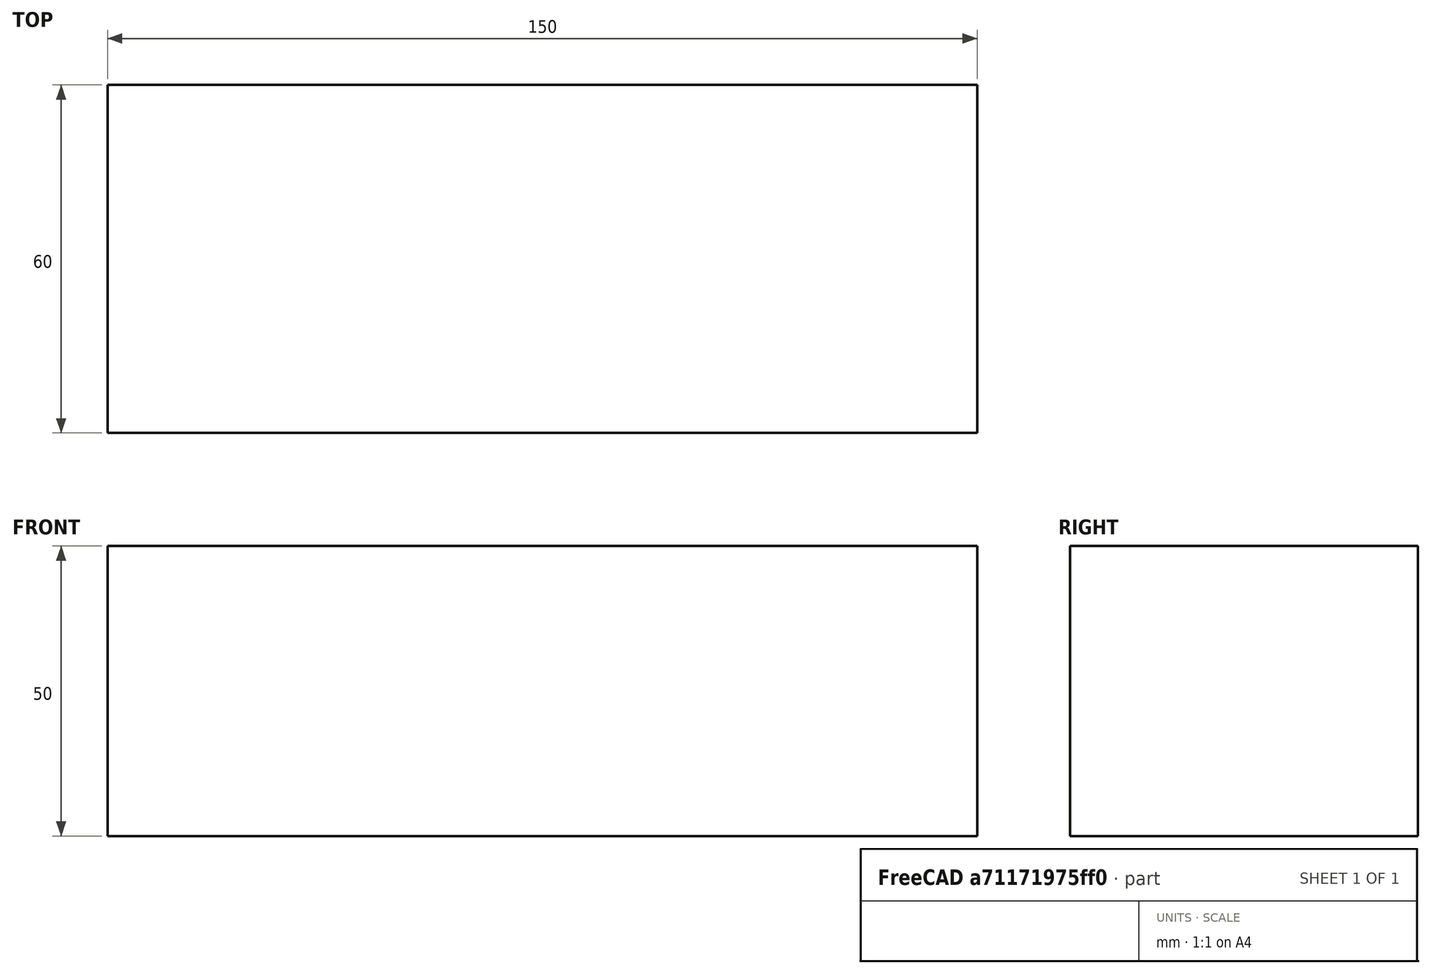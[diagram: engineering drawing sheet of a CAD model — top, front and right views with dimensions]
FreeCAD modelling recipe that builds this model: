
FCSTD DOCUMENT  (FreeCAD 0.15R4671 (Git))
Label: Flat Bar 150x60 EN10058 S235JR
License: All rights reserved
LicenseURL: http://en.wikipedia.org/wiki/All_rights_reserved
objects: Sketcher::SketchObject×1, Part::Extrusion×1
note: 2 computed .brp shape members not serialized (recipe doc carries the construction recipe); baked Part::Feature solids carry a one-line shape summary decoded from their .brp

FEATURE [Sketcher::SketchObject] Sketch
  sketch-geometry (4):
    g0: LineSegment StartX=-75 StartY=-30 StartZ=0 EndX=75 EndY=-30 EndZ=0
    g1: LineSegment StartX=75 StartY=-30 StartZ=0 EndX=75 EndY=30 EndZ=0
    g2: LineSegment StartX=75 StartY=30 StartZ=0 EndX=-75 EndY=30 EndZ=0
    g3: LineSegment StartX=-75 StartY=30 StartZ=0 EndX=-75 EndY=-30 EndZ=0
  constraints (12):
    c: Coincident(g0,g1)
    c: Coincident(g1,g2)
    c: Coincident(g2,g3)
    c: Coincident(g3,g0)
    c: Horizontal(g0)
    c: Horizontal(g2)
    c: Vertical(g1)
    c: Vertical(g3)
    c: Symmetric(g1,g2,g-2)
    c: Symmetric(g0,g1,g-1)
    c: DistanceY(g1) = 60
    c: DistanceX(g0) = 150
FEATURE [Part::Extrusion] Extrude  label="Flat Bar 150x60 EN10058 S235JR"
  Base = -> Sketch
  Dir = (0,0,50)
  Solid = true
